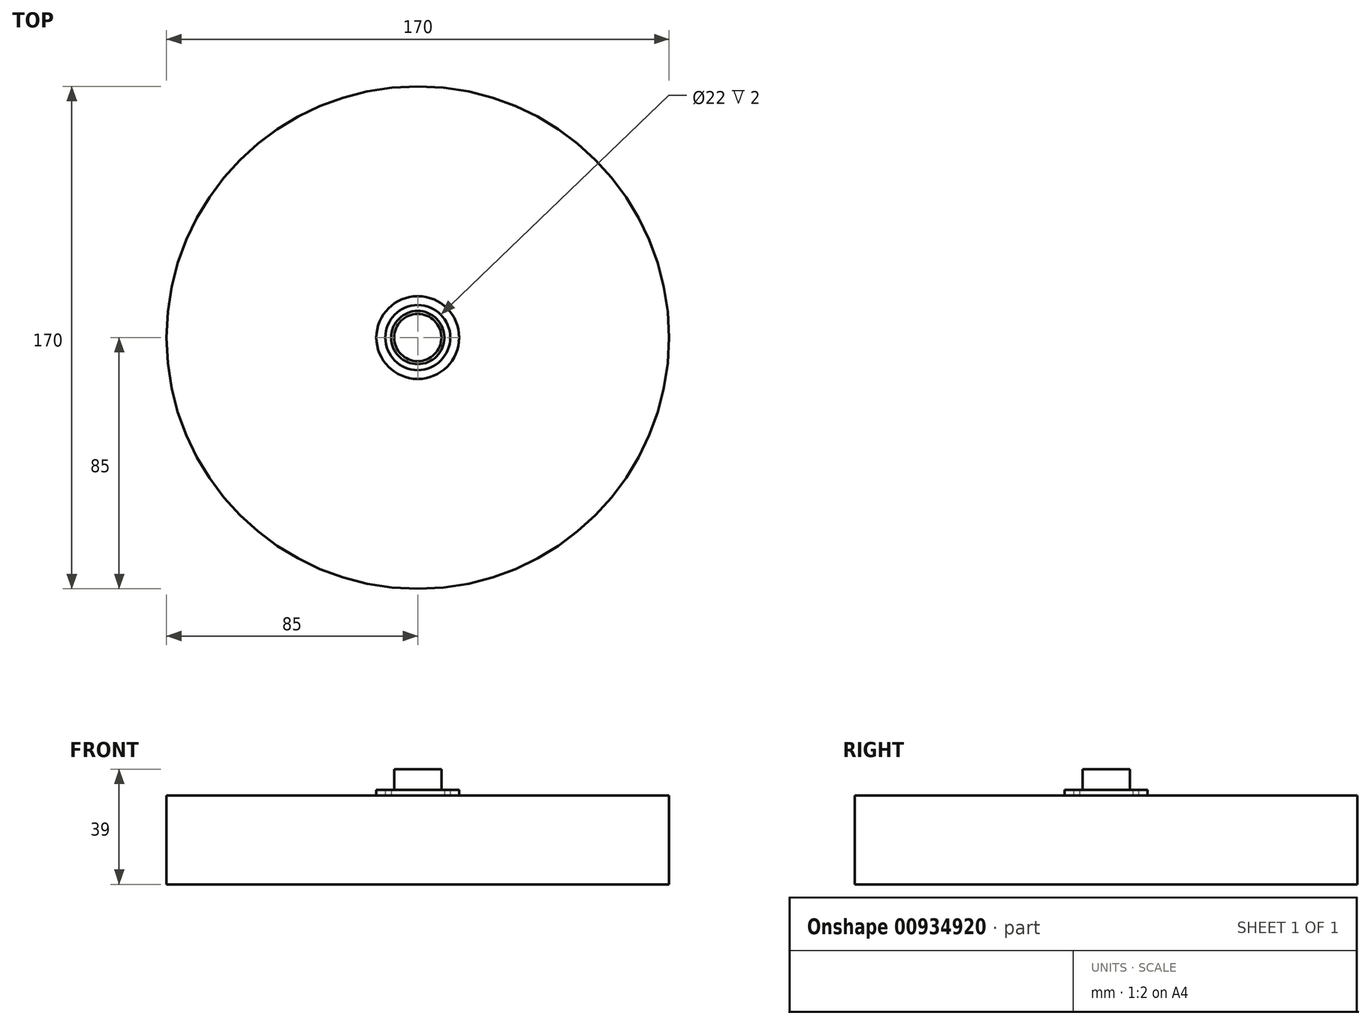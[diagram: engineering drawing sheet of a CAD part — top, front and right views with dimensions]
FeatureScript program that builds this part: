
annotation { "Feature Type Name" : "Feature", "Feature Type Description" : "" }
export const myFeature = defineFeature(function(context is Context, id is Id, definition is map)
    precondition{}
    {
        {
            var Q0;
            Q0=qCreatedBy(makeId("Top.planeOp"),FACE);
            var sketch = newSketch(context, id + "F0", { "sketchPlane" : qUnion([Q0])});
            skCircle(sketch, "E0", {"center": v(0, 0) * mm, "radius": 50 * mm});
            skCircle(sketch, "E1", {"center": v(0, 0) * mm, "radius": 14 * mm});
            skCircle(sketch, "E2", {"center": v(0, 0) * mm, "radius": 11 * mm});
            skSolve(sketch);
        }
        {
            var Q0;
            Q0=makeQuery(id+"F0.imprint","IMPRINT",FACE,{"disambiguationData":[TD([[makeQuery(id+"F0.imprint","IMPRINT",EDGE,{"derivedFrom":sQuery(id+"F0.wireOp",EDGE,"E2")}),1.0]])]});
            extrude(context, id + "F1", {"entities" : qUnion([Q0]), "depth" : 25 * mm, "offsetDistance" : 25 * mm});
        }
        {
            var Q0;
            Q0=makeQuery(id+"F0.imprint","IMPRINT",FACE,{"disambiguationData":[TD([[makeQuery(id+"F0.imprint","IMPRINT",EDGE,{"derivedFrom":sQuery(id+"F0.wireOp",EDGE,"E1")}),1.0]])]});
            extrude(context, id + "F2", {"entities" : qUnion([Q0]), "operationType" : NewBodyOperationType.ADD, "depth" : 32 * mm, "offsetDistance" : 25 * mm});
        }
        {
            var Q0;
            Q0=makeQuery(id+"F0.imprint","IMPRINT",FACE,{"disambiguationData":[TD([[makeQuery(id+"F0.imprint","IMPRINT",EDGE,{"derivedFrom":sQuery(id+"F0.wireOp",EDGE,"E0")}),1.0]])]});
            extrude(context, id + "F3", {"entities" : qUnion([Q0]), "operationType" : NewBodyOperationType.ADD, "depth" : 25 * mm, "offsetDistance" : 25 * mm});
        }
        {
            var Q0;
            Q0=qCreatedBy(makeId("Top.planeOp"),FACE);
            var sketch = newSketch(context, id + "F4", { "sketchPlane" : qUnion([Q0])});
            skCircle(sketch, "E3", {"center": v(0, 0) * mm, "radius": 85 * mm});
            skCircle(sketch, "E4", {"center": v(0, 0) * mm, "radius": 9 * mm});
            skCircle(sketch, "E5", {"center": v(0, 0) * mm, "radius": 8 * mm});
            skSolve(sketch);
        }
        {
            var Q0;
            Q0=makeQuery(id+"F4.imprint","IMPRINT",FACE,{"disambiguationData":[TD([[makeQuery(id+"F4.imprint","IMPRINT",EDGE,{"derivedFrom":sQuery(id+"F4.wireOp",EDGE,"E5")}),1.0]])]});
            extrude(context, id + "F5", {"entities" : qUnion([Q0]), "depth" : 39 * mm, "offsetDistance" : 25 * mm});
        }
        {
            var Q0;
            Q0=makeQuery(id+"F4.imprint","IMPRINT",FACE,{"disambiguationData":[TD([[makeQuery(id+"F4.imprint","IMPRINT",EDGE,{"derivedFrom":sQuery(id+"F4.wireOp",EDGE,"E4")}),1.0]])]});
            extrude(context, id + "F6", {"entities" : qUnion([Q0]), "operationType" : NewBodyOperationType.ADD, "depth" : 32 * mm, "offsetDistance" : 25 * mm});
        }
        {
            var Q0;
            Q0=makeQuery(id+"F4.imprint","IMPRINT",FACE,{"disambiguationData":[TD([[makeQuery(id+"F4.imprint","IMPRINT",EDGE,{"derivedFrom":sQuery(id+"F4.wireOp",EDGE,"E3")}),1.0]])]});
            extrude(context, id + "F7", {"entities" : qUnion([Q0]), "operationType" : NewBodyOperationType.ADD, "depth" : 30 * mm, "offsetDistance" : 25 * mm});
        }
    });
